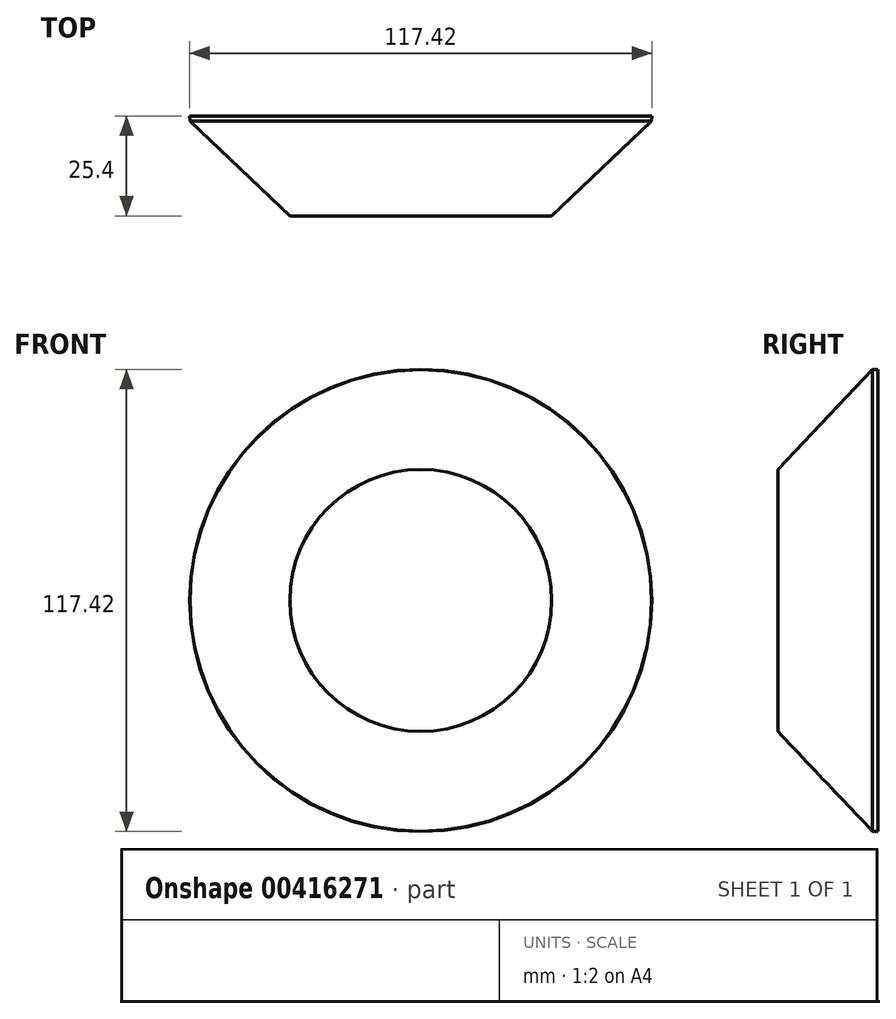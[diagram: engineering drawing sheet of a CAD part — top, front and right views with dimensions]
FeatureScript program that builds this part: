
annotation { "Feature Type Name" : "Feature", "Feature Type Description" : "" }
export const myFeature = defineFeature(function(context is Context, id is Id, definition is map)
    precondition{}
    {
        {
            var Q0;
            Q0=qCreatedBy(makeId("Front.planeOp"),FACE);
            var sketch = newSketch(context, id + "F0", { "sketchPlane" : qUnion([Q0])});
            skCircle(sketch, "E0", {"center": v(0, 0) * mm, "radius": 57.38 * mm});
            skSolve(sketch);
        }
        {
            var Q0;
            Q0 = qSketchRegion(id + "F0", true);
            extrude(context, id + "F1", {"entities" : qUnion([Q0]), "oppositeDirection" : true, "depth" : 25.4 * mm, "hasDraft" : true, "draftAngle" : 3 * degree});
        }
        {
            var Q0;
            Q0=makeQuery(id+"F1.opExtrude","CAP_FACE",FACE,{"disambiguationData":[OSD([sQuery(id+"F0.wireOp",EDGE,"E0")])],"isStart":true});
            chamfer(context, id + "F2", {"entities" : qUnion([Q0]), "width" : 25.4 * mm, "tangentPropagation" : true});
        }
    });
